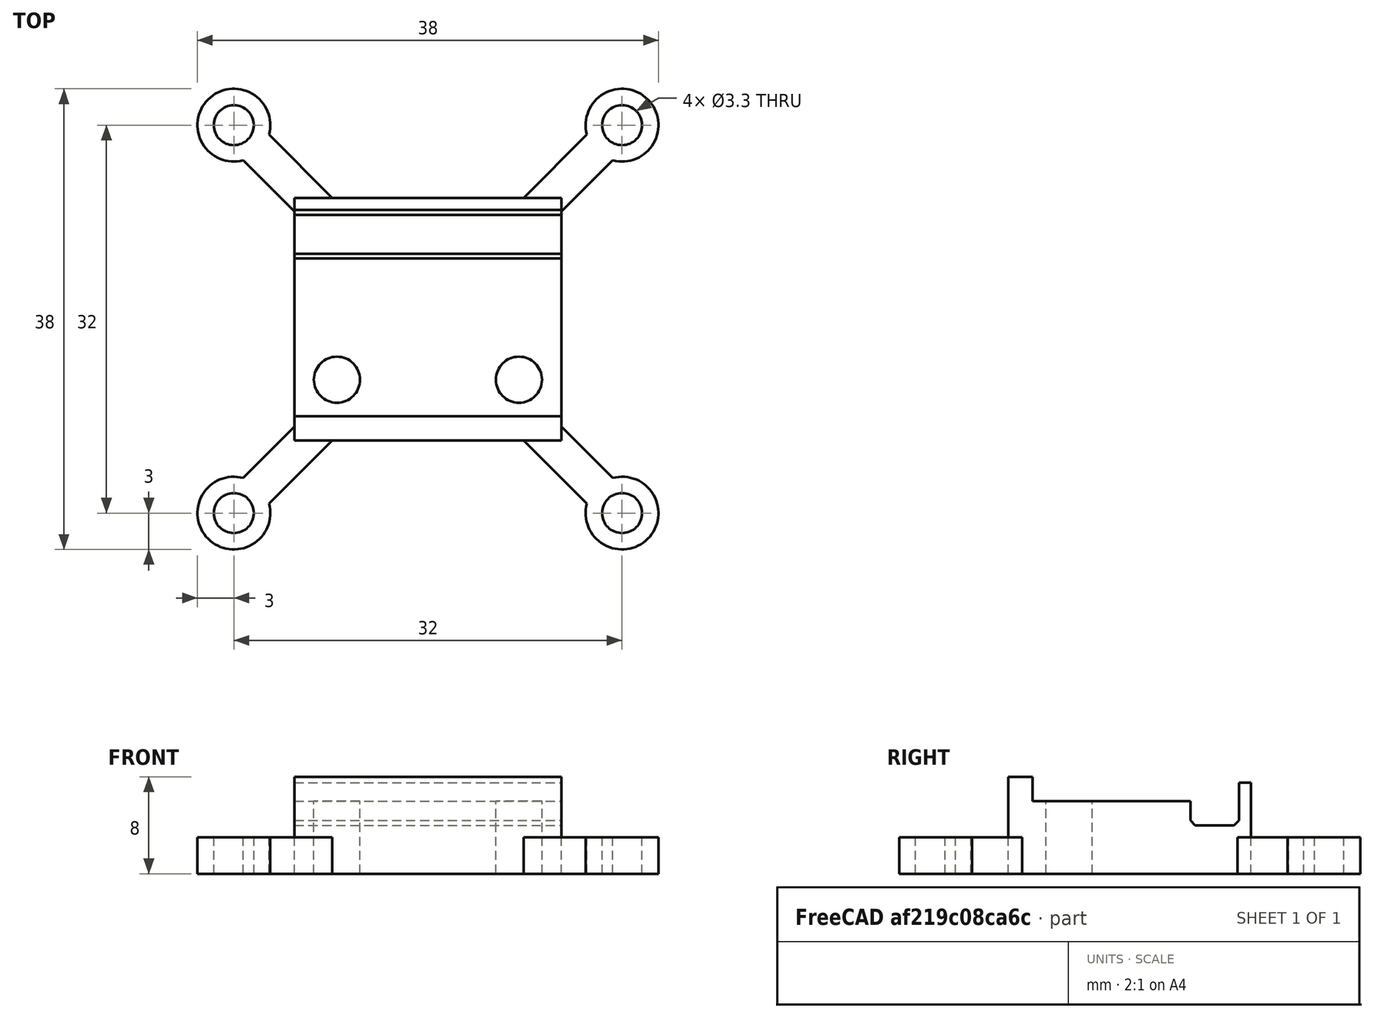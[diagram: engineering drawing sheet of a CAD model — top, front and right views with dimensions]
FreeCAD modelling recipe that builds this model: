
FCSTD DOCUMENT  (FreeCAD 0.19R24291 (Git))
Label: adxl345-mount
License: Other
LicenseURL: GPL3
objects: Part::Cylinder×6, Part::MultiFuse×3, Part::Feature×2, Part::Cut×2, Part::Extrusion×1
note: 14 computed .brp shape members not serialized (recipe doc carries the construction recipe); baked Part::Feature solids carry a one-line shape summary decoded from their .brp

FEATURE [Part::Feature] Cut010001001
  Placement = pos=(0,-8,8) rot=(0,0,1;0rad)
  shape: bbox 22 x 20 x 5 mm, 16 faces (baked)
FEATURE [Part::Cylinder] Cylinder
  Angle = 360
  AttacherType = Attacher::AttachEngine3D
  Height = 10
  Placement = pos=(16,16,0) rot=(0,0,1;0rad)
  Radius = 1.65
FEATURE [Part::Cylinder] Cylinder001
  Angle = 360
  AttacherType = Attacher::AttachEngine3D
  Height = 10
  Placement = pos=(-16,16,0) rot=(0,0,1;0rad)
  Radius = 1.65
FEATURE [Part::Cylinder] Cylinder002
  Angle = 360
  AttacherType = Attacher::AttachEngine3D
  Height = 10
  Placement = pos=(-16,-16,0) rot=(0,0,1;0rad)
  Radius = 1.65
FEATURE [Part::Cylinder] Cylinder003
  Angle = 360
  AttacherType = Attacher::AttachEngine3D
  Height = 10
  Placement = pos=(16,-16,0) rot=(0,0,1;0rad)
  Radius = 1.65
FEATURE [Part::Feature] Fusion002001_cs
  shape: bbox 38 x 38 x 3e-07 mm, 0 faces, 0 solids (baked)
FEATURE [Part::Extrusion] Extrude
  Base = -> Fusion002001_cs
  Dir = (0,0,1)
  DirMode = 2
  FaceMakerClass = Part::FaceMakerBullseye
  LengthFwd = 3
  LengthRev = 0
  Solid = true
  Symmetric = false
FEATURE [Part::MultiFuse] Fusion
  Shapes = -> [Cylinder003,Cylinder,Cylinder001,Cylinder002]
FEATURE [Part::Cut] Cut
  Base = -> Extrude
  Tool = -> Fusion
FEATURE [Part::MultiFuse] Fusion001
  Shapes = -> [Cut,Cut010001001]
FEATURE [Part::Cylinder] Cylinder004
  Angle = 360
  AttacherType = Attacher::AttachEngine3D
  Height = 10
  Placement = pos=(7.5,-5,0) rot=(0,0,1;0rad)
  Radius = 1.9
FEATURE [Part::Cylinder] Cylinder005
  Angle = 360
  AttacherType = Attacher::AttachEngine3D
  Height = 10
  Placement = pos=(-7.5,-5,0) rot=(0,0,1;0rad)
  Radius = 1.9
FEATURE [Part::MultiFuse] Fusion002
  Shapes = -> [Cylinder005,Cylinder004]
FEATURE [Part::Cut] Cut010001002
  Base = -> Fusion001
  Tool = -> Fusion002
